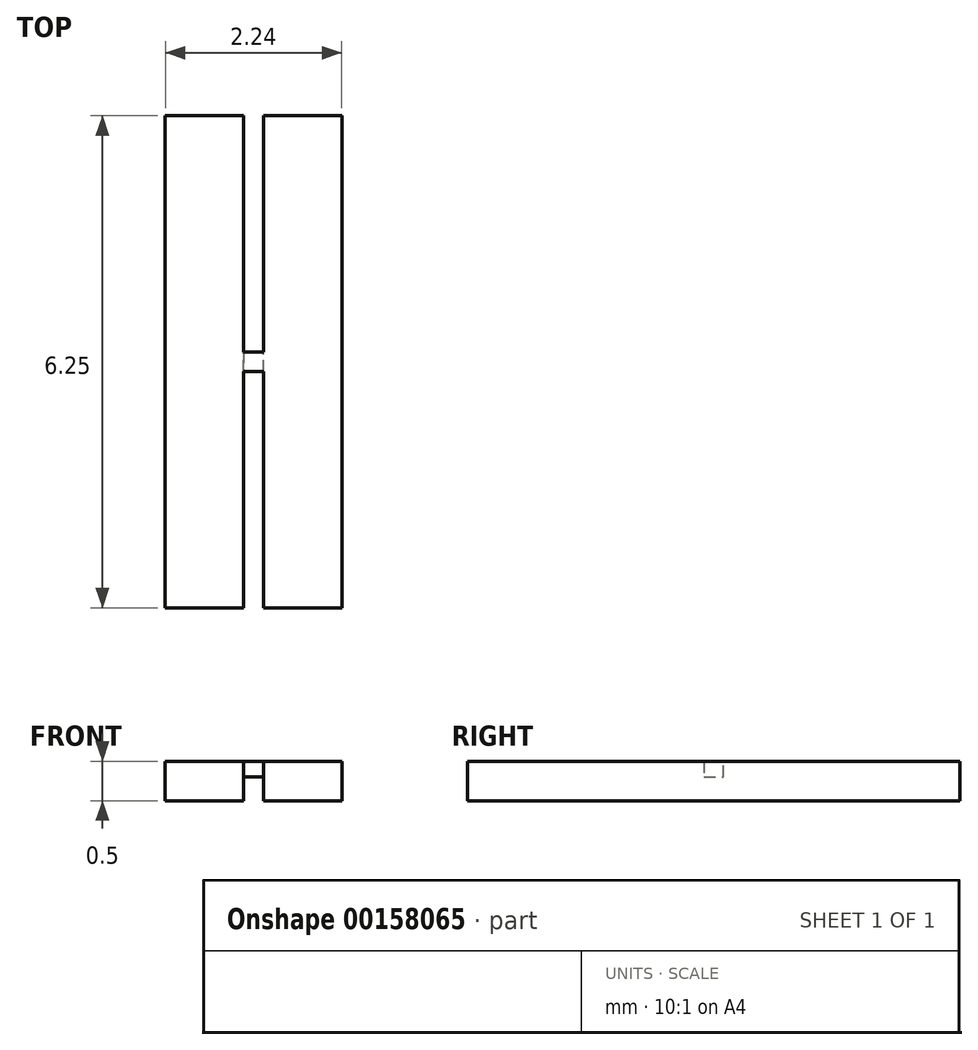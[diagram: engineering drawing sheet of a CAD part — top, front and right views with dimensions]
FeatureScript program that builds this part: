
annotation { "Feature Type Name" : "Feature", "Feature Type Description" : "" }
export const myFeature = defineFeature(function(context is Context, id is Id, definition is map)
    precondition{}
    {
        {
            var Q0;
            Q0=qCreatedBy(makeId("Right.planeOp"),FACE);
            var sketch = newSketch(context, id + "F0", { "sketchPlane" : qUnion([Q0])});
            skLineSegment(sketch, "E0.bottom", {"start": v(0, 0) * mm, "end": v(0.25, 0) * mm});
            skLineSegment(sketch, "E0.top", {"start": v(0, 0.2) * mm, "end": v(0.25, 0.2) * mm});
            skLineSegment(sketch, "E0.left", {"start": v(0, 0) * mm, "end": v(0, 0.2) * mm});
            skLineSegment(sketch, "E0.right", {"start": v(0.25, 0) * mm, "end": v(0.25, 0.2) * mm});
            skSolve(sketch);
        }
        {
            var Q0;
            Q0=qSketchRegion(id+"F0",true);
            extrude(context, id + "F1", {"entities" : qUnion([Q0]), "endBound" : BoundingType.SYMMETRIC, "depth" : .25 * mm});
        }
        {
            var Q0;
            Q0=makeQuery(id+"F1.opExtrude","CAP_FACE",FACE,{"disambiguationData":[OSD([sQuery(id+"F0.wireOp",EDGE,"E0.bottom"),sQuery(id+"F0.wireOp",EDGE,"E0.top"),sQuery(id+"F0.wireOp",EDGE,"E0.left"),sQuery(id+"F0.wireOp",EDGE,"E0.right")])],"isStart":false});
            var sketch = newSketch(context, id + "F2", { "sketchPlane" : qUnion([Q0])});
            skLineSegment(sketch, "E1.bottom", {"start": v(0, 0.2) * mm, "end": v(0.25, 0.2) * mm});
            skLineSegment(sketch, "E1.top", {"start": v(0, -0.3) * mm, "end": v(0.25, -0.3) * mm});
            skLineSegment(sketch, "E1.left", {"start": v(0, 0.2) * mm, "end": v(0, -0.3) * mm});
            skLineSegment(sketch, "E1.right", {"start": v(0.25, 0.2) * mm, "end": v(0.25, -0.3) * mm});
            skSolve(sketch);
        }
        {
            var Q0;
            Q0=qSketchRegion(id+"F2",true);
            extrude(context, id + "F3", {"entities" : qUnion([Q0]), "operationType" : NewBodyOperationType.ADD, "depth" : 1 * mm});
        }
        {
            var Q0;
            Q0=makeQuery(id+"F1.opExtrude","CAP_FACE",FACE,{"disambiguationData":[OSD([sQuery(id+"F0.wireOp",EDGE,"E0.bottom"),sQuery(id+"F0.wireOp",EDGE,"E0.top"),sQuery(id+"F0.wireOp",EDGE,"E0.left"),sQuery(id+"F0.wireOp",EDGE,"E0.right")])],"isStart":true});
            var sketch = newSketch(context, id + "F4", { "sketchPlane" : qUnion([Q0])});
            skLineSegment(sketch, "E2.bottom", {"start": v(-0.25, 0.2) * mm, "end": v(0, 0.2) * mm});
            skLineSegment(sketch, "E2.top", {"start": v(-0.25, -0.3) * mm, "end": v(0, -0.3) * mm});
            skLineSegment(sketch, "E2.left", {"start": v(-0.25, 0.2) * mm, "end": v(-0.25, -0.3) * mm});
            skLineSegment(sketch, "E2.right", {"start": v(0, 0.2) * mm, "end": v(0, -0.3) * mm});
            skSolve(sketch);
        }
        {
            var Q0;
            Q0=qSketchRegion(id+"F4",true);
            extrude(context, id + "F5", {"entities" : qUnion([Q0]), "operationType" : NewBodyOperationType.ADD, "depth" : 1 * mm});
        }
        {
            var Q0;
            Q0=makeQuery(id+"F5.boolean.opBoolean","MERGE",FACE,{"derivedFrom":[makeQuery(id+"F3.boolean.opBoolean","MERGE",FACE,{"derivedFrom":[makeQuery(id+"F1.opExtrude","SWEPT_FACE",FACE,{"disambiguationData":[OSD([sQuery(id+"F0.wireOp",EDGE,"E0.right")])]}),makeQuery(id+"F3.opExtrude","SWEPT_FACE",FACE,{"disambiguationData":[OSD([sQuery(id+"F2.wireOp",EDGE,"E1.right")])]})]}),makeQuery(id+"F5.opExtrude","SWEPT_FACE",FACE,{"disambiguationData":[OSD([sQuery(id+"F4.wireOp",EDGE,"E2.left")])]})]});
            var sketch = newSketch(context, id + "F6", { "sketchPlane" : qUnion([Q0])});
            skLineSegment(sketch, "E3.bottom", {"start": v(-0.12, -0.3) * mm, "end": v(-1.13, -0.3) * mm});
            skLineSegment(sketch, "E3.top", {"start": v(-0.13, 0.2) * mm, "end": v(-1.13, 0.2) * mm});
            skLineSegment(sketch, "E3.left", {"start": v(-0.12, -0.3) * mm, "end": v(-0.13, 0.2) * mm});
            skLineSegment(sketch, "E3.right", {"start": v(-1.13, -0.3) * mm, "end": v(-1.13, 0.2) * mm});
            skLineSegment(sketch, "E4.bottom", {"start": v(0.12, -0.3) * mm, "end": v(1.13, -0.3) * mm});
            skLineSegment(sketch, "E4.top", {"start": v(0.12, 0.2) * mm, "end": v(1.13, 0.2) * mm});
            skLineSegment(sketch, "E4.left", {"start": v(0.12, -0.3) * mm, "end": v(0.12, 0.2) * mm});
            skLineSegment(sketch, "E4.right", {"start": v(1.13, -0.3) * mm, "end": v(1.13, 0.2) * mm});
            skSolve(sketch);
        }
        {
            var Q0;
            Q0=qSketchRegion(id+"F6",true);
            extrude(context, id + "F7", {"entities" : qUnion([Q0]), "operationType" : NewBodyOperationType.ADD, "depth" : 3 * mm});
        }
        {
            var Q0;
            Q0=makeQuery(id+"F5.boolean.opBoolean","MERGE",FACE,{"derivedFrom":[makeQuery(id+"F3.boolean.opBoolean","MERGE",FACE,{"derivedFrom":[makeQuery(id+"F1.opExtrude","SWEPT_FACE",FACE,{"disambiguationData":[OSD([sQuery(id+"F0.wireOp",EDGE,"E0.left")])]}),makeQuery(id+"F3.opExtrude","SWEPT_FACE",FACE,{"disambiguationData":[OSD([sQuery(id+"F2.wireOp",EDGE,"E1.left")])]})]}),makeQuery(id+"F5.opExtrude","SWEPT_FACE",FACE,{"disambiguationData":[OSD([sQuery(id+"F4.wireOp",EDGE,"E2.right")])]})]});
            var sketch = newSketch(context, id + "F8", { "sketchPlane" : qUnion([Q0])});
            skLineSegment(sketch, "E5.bottom", {"start": v(-0.12, -0.3) * mm, "end": v(-1.13, -0.3) * mm});
            skLineSegment(sketch, "E5.top", {"start": v(-0.13, 0.2) * mm, "end": v(-1.13, 0.2) * mm});
            skLineSegment(sketch, "E5.left", {"start": v(-0.12, -0.3) * mm, "end": v(-0.13, 0.2) * mm});
            skLineSegment(sketch, "E5.right", {"start": v(-1.13, -0.3) * mm, "end": v(-1.13, 0.2) * mm});
            skLineSegment(sketch, "E6.bottom", {"start": v(1.13, 0.2) * mm, "end": v(0.12, 0.2) * mm});
            skLineSegment(sketch, "E6.top", {"start": v(1.13, -0.3) * mm, "end": v(0.12, -0.3) * mm});
            skLineSegment(sketch, "E6.left", {"start": v(1.13, 0.2) * mm, "end": v(1.13, -0.3) * mm});
            skLineSegment(sketch, "E6.right", {"start": v(0.12, 0.2) * mm, "end": v(0.12, -0.3) * mm});
            skSolve(sketch);
        }
        {
            var Q0;
            Q0=qSketchRegion(id+"F8",true);
            extrude(context, id + "F9", {"entities" : qUnion([Q0]), "operationType" : NewBodyOperationType.ADD, "depth" : 3 * mm});
        }
    });
